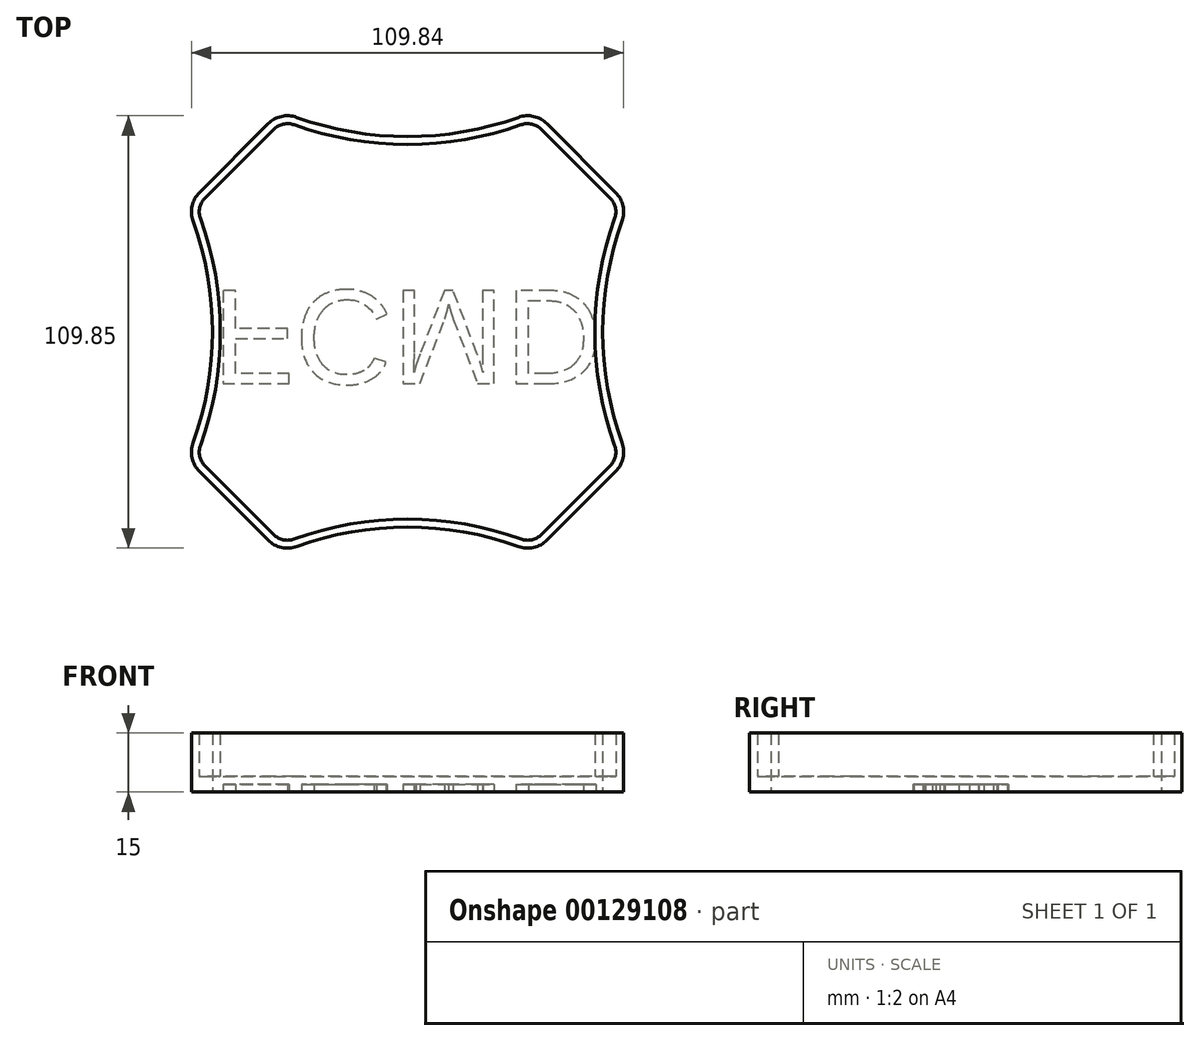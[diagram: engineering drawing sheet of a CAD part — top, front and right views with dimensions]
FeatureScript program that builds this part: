
annotation { "Feature Type Name" : "Feature", "Feature Type Description" : "" }
export const myFeature = defineFeature(function(context is Context, id is Id, definition is map)
    precondition{}
    {
        {
            var Q0;
            Q0=qCreatedBy(makeId("Top.planeOp"),FACE);
            var sketch = newSketch(context, id + "F0", { "sketchPlane" : qUnion([Q0])});
            skPoint(sketch, "E0.middle", {"position": v(0, 0) * mm});
            skLineSegment(sketch, "E1", {"start": v(34.03, 51.47) * mm, "end": v(51.46, 34.04) * mm});
            skLineSegment(sketch, "E2", {"start": v(51.46, -34.04) * mm, "end": v(34.04, -51.46) * mm});
            skLineSegment(sketch, "E3", {"start": v(-34.04, -51.46) * mm, "end": v(-51.45, -34.05) * mm});
            skLineSegment(sketch, "E4", {"start": v(-51.45, 34.05) * mm, "end": v(-34.03, 51.47) * mm});
            skArc(sketch, "E5", {"start": v(52.62, 28.8) * mm, "mid": v(47.57, 0) * mm, "end": v(52.62, -28.8) * mm});
            skArc(sketch, "E6", {"start": v(28.8, -52.62) * mm, "mid": v(0, -47.57) * mm, "end": v(-28.8, -52.62) * mm});
            skArc(sketch, "E7", {"start": v(-52.62, -28.8) * mm, "mid": v(-47.56, 0) * mm, "end": v(-52.62, 28.8) * mm});
            skArc(sketch, "E8", {"start": v(-28.81, 52.64) * mm, "mid": v(0, 47.63) * mm, "end": v(28.81, 52.64) * mm});
            skPoint(sketch, "E9.visualSharp", {"position": v(-31.75, 53.75) * mm});
            skArc(sketch, "E9.filletArc", {"start": v(-28.81, 52.64) * mm, "mid": v(-31.6, 52.8) * mm, "end": v(-34.03, 51.47) * mm});
            skPoint(sketch, "E10.visualSharp", {"position": v(31.75, 53.75) * mm});
            skArc(sketch, "E10.filletArc", {"start": v(34.03, 51.47) * mm, "mid": v(31.6, 52.8) * mm, "end": v(28.81, 52.64) * mm});
            skPoint(sketch, "E11.visualSharp", {"position": v(53.75, 31.75) * mm});
            skArc(sketch, "E11.filletArc", {"start": v(52.62, 28.8) * mm, "mid": v(52.8, 31.6) * mm, "end": v(51.46, 34.04) * mm});
            skPoint(sketch, "E12.visualSharp", {"position": v(53.75, -31.75) * mm});
            skArc(sketch, "E12.filletArc", {"start": v(51.46, -34.04) * mm, "mid": v(52.8, -31.6) * mm, "end": v(52.62, -28.8) * mm});
            skPoint(sketch, "E13.visualSharp", {"position": v(31.75, -53.75) * mm});
            skArc(sketch, "E13.filletArc", {"start": v(28.8, -52.62) * mm, "mid": v(31.6, -52.8) * mm, "end": v(34.04, -51.46) * mm});
            skPoint(sketch, "E14.visualSharp", {"position": v(-53.75, -31.75) * mm});
            skArc(sketch, "E14.filletArc", {"start": v(-52.62, -28.8) * mm, "mid": v(-52.8, -31.6) * mm, "end": v(-51.45, -34.05) * mm});
            skPoint(sketch, "E15.visualSharp", {"position": v(-31.75, -53.75) * mm});
            skArc(sketch, "E15.filletArc", {"start": v(-34.04, -51.46) * mm, "mid": v(-31.6, -52.8) * mm, "end": v(-28.8, -52.62) * mm});
            skPoint(sketch, "E16.visualSharp", {"position": v(-53.75, 31.75) * mm});
            skArc(sketch, "E16.filletArc", {"start": v(-51.45, 34.05) * mm, "mid": v(-52.8, 31.6) * mm, "end": v(-52.62, 28.8) * mm});
            skArc(sketch, "E17.0", {"start": v(-28.14, 54.52) * mm, "mid": v(0, 49.63) * mm, "end": v(28.14, 54.52) * mm});
            skLineSegment(sketch, "E18.0", {"start": v(35.45, 52.88) * mm, "end": v(52.87, 35.46) * mm});
            skArc(sketch, "E19.0", {"start": v(54.5, 28.13) * mm, "mid": v(49.57, 0) * mm, "end": v(54.5, -28.13) * mm});
            skLineSegment(sketch, "E20.0", {"start": v(52.87, -35.46) * mm, "end": v(35.46, -52.87) * mm});
            skArc(sketch, "E21.0", {"start": v(28.13, -54.5) * mm, "mid": v(0, -49.57) * mm, "end": v(-28.13, -54.5) * mm});
            skLineSegment(sketch, "E22.0", {"start": v(-35.46, -52.87) * mm, "end": v(-52.87, -35.46) * mm});
            skArc(sketch, "E23.0", {"start": v(-54.5, -28.12) * mm, "mid": v(-49.56, 0) * mm, "end": v(-54.5, 28.12) * mm});
            skLineSegment(sketch, "E24.0", {"start": v(-52.87, 35.46) * mm, "end": v(-35.45, 52.88) * mm});
            skArc(sketch, "E25.0", {"start": v(-28.14, 54.52) * mm, "mid": v(-32.03, 54.76) * mm, "end": v(-35.45, 52.88) * mm});
            skArc(sketch, "E26.0", {"start": v(35.45, 52.88) * mm, "mid": v(32.03, 54.76) * mm, "end": v(28.14, 54.52) * mm});
            skArc(sketch, "E27.0", {"start": v(54.5, 28.13) * mm, "mid": v(54.75, 32.03) * mm, "end": v(52.87, 35.46) * mm});
            skArc(sketch, "E28.0", {"start": v(52.87, -35.46) * mm, "mid": v(54.75, -32.03) * mm, "end": v(54.5, -28.13) * mm});
            skArc(sketch, "E29.0", {"start": v(28.13, -54.5) * mm, "mid": v(32.03, -54.75) * mm, "end": v(35.46, -52.87) * mm});
            skArc(sketch, "E30.0", {"start": v(-35.46, -52.87) * mm, "mid": v(-32.03, -54.75) * mm, "end": v(-28.13, -54.5) * mm});
            skArc(sketch, "E31.0", {"start": v(-54.5, -28.12) * mm, "mid": v(-54.75, -32.03) * mm, "end": v(-52.87, -35.46) * mm});
            skArc(sketch, "E32.0", {"start": v(-52.87, 35.46) * mm, "mid": v(-54.75, 32.03) * mm, "end": v(-54.5, 28.12) * mm});
            skSolve(sketch);
        }
        {
            var Q0;
            Q0=makeQuery(id+"F0.imprint","IMPRINT",FACE,{"disambiguationData":[TD([[makeQuery(id+"F0.imprint","IMPRINT",EDGE,{"derivedFrom":sQuery(id+"F0.wireOp",EDGE,"E1")}),-1.0]])]});
            extrude(context, id + "F1", {"entities" : qUnion([Q0]), "depth" : 4 * mm});
        }
        {
            var Q0;
            Q0 = qSketchRegion(id + "F0", true);
            extrude(context, id + "F2", {"entities" : qUnion([Q0]), "operationType" : NewBodyOperationType.ADD, "depth" : 15 * mm});
        }
        {
            var Q0;
            {var subQ0=sQuery(id+"F0.wireOp",EDGE,"E16.filletArc");var subQ1=sQuery(id+"F0.wireOp",EDGE,"E15.filletArc");var subQ2=sQuery(id+"F0.wireOp",EDGE,"E14.filletArc");var subQ3=sQuery(id+"F0.wireOp",EDGE,"E13.filletArc");var subQ4=sQuery(id+"F0.wireOp",EDGE,"E12.filletArc");var subQ5=sQuery(id+"F0.wireOp",EDGE,"E11.filletArc");var subQ6=sQuery(id+"F0.wireOp",EDGE,"E10.filletArc");var subQ7=sQuery(id+"F0.wireOp",EDGE,"E9.filletArc");var subQ8=sQuery(id+"F0.wireOp",EDGE,"E8");var subQ9=sQuery(id+"F0.wireOp",EDGE,"E7");var subQ10=sQuery(id+"F0.wireOp",EDGE,"E6");var subQ11=sQuery(id+"F0.wireOp",EDGE,"E5");var subQ12=sQuery(id+"F0.wireOp",EDGE,"E4");var subQ13=sQuery(id+"F0.wireOp",EDGE,"E3");var subQ14=sQuery(id+"F0.wireOp",EDGE,"E2");var subQ15=sQuery(id+"F0.wireOp",EDGE,"E1");Q0=makeQuery(id+"F2.boolean.opBoolean","MERGE",FACE,{"derivedFrom":[makeQuery(id+"F1.opExtrude","CAP_FACE",FACE,{"disambiguationData":[OSD([subQ15,subQ14,subQ13,subQ12,subQ11,subQ10,subQ9,subQ8,subQ7,subQ6,subQ5,subQ4,subQ3,subQ2,subQ1,subQ0])],"isStart":true}),makeQuery(id+"F2.opExtrude","CAP_FACE",FACE,{"disambiguationData":[OSD([subQ15,subQ14,subQ13,subQ12,subQ11,subQ10,subQ9,subQ8,subQ7,subQ6,subQ5,subQ4,subQ3,subQ2,subQ1,subQ0,sQuery(id+"F0.wireOp",EDGE,"E17.0"),sQuery(id+"F0.wireOp",EDGE,"E18.0"),sQuery(id+"F0.wireOp",EDGE,"E19.0"),sQuery(id+"F0.wireOp",EDGE,"E20.0"),sQuery(id+"F0.wireOp",EDGE,"E21.0"),sQuery(id+"F0.wireOp",EDGE,"E22.0"),sQuery(id+"F0.wireOp",EDGE,"E23.0"),sQuery(id+"F0.wireOp",EDGE,"E24.0"),sQuery(id+"F0.wireOp",EDGE,"E25.0"),sQuery(id+"F0.wireOp",EDGE,"E26.0"),sQuery(id+"F0.wireOp",EDGE,"E27.0"),sQuery(id+"F0.wireOp",EDGE,"E28.0"),sQuery(id+"F0.wireOp",EDGE,"E29.0"),sQuery(id+"F0.wireOp",EDGE,"E30.0"),sQuery(id+"F0.wireOp",EDGE,"E31.0"),sQuery(id+"F0.wireOp",EDGE,"E32.0")])],"isStart":true})]});}
            var sketch = newSketch(context, id + "F3", { "sketchPlane" : qUnion([Q0])});
            skLineSegment(sketch, "E33", {"start": v(0, 49.57) * mm, "end": v(0, -49.63) * mm, "construction": true});
            skLineSegment(sketch, "E34", {"start": v(-49.56, 0) * mm, "end": v(49.57, 0) * mm, "construction": true});
            skText(sketch, "E35", { "text": "FCMD", "fontName": "Arimo-Regular.ttf"});
            const initialGuessF3  = {"E35": [-0.0497, -0.0105, 1, 0, 0.02474]};
            skSetInitialGuess(sketch, initialGuessF3);
            skSolve(sketch);
        }
        {
            var Q0;
            Q0 = qSketchRegion(id + "F3", true);
            extrude(context, id + "F4", {"entities" : qUnion([Q0]), "operationType" : NewBodyOperationType.REMOVE, "oppositeDirection" : true, "depth" : 2 * mm});
        }
    });
